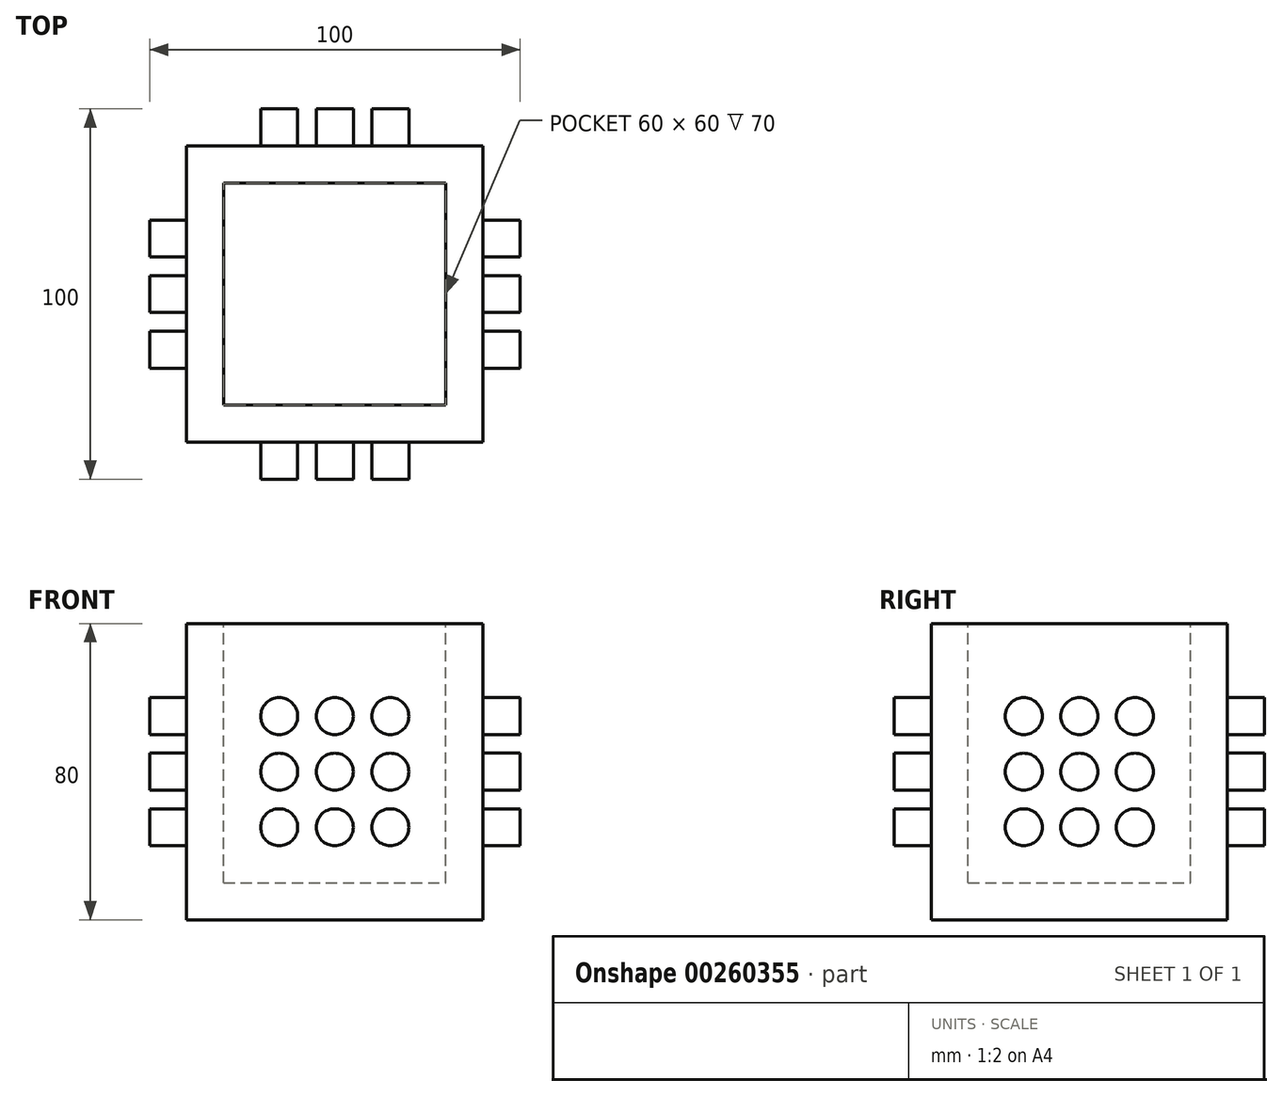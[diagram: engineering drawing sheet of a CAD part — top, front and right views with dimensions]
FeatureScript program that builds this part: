
annotation { "Feature Type Name" : "Feature", "Feature Type Description" : "" }
export const myFeature = defineFeature(function(context is Context, id is Id, definition is map)
    precondition{}
    {
        {
            var Q0;
            Q0=qCreatedBy(makeId("Front.planeOp"),FACE);
            var sketch = newSketch(context, id + "F0", { "sketchPlane" : qUnion([Q0])});
            skLineSegment(sketch, "E0.bottom", {"start": v(0, 0) * mm, "end": v(80, 0) * mm});
            skLineSegment(sketch, "E0.top", {"start": v(0, 80) * mm, "end": v(80, 80) * mm});
            skLineSegment(sketch, "E0.left", {"start": v(0, 0) * mm, "end": v(0, 80) * mm});
            skLineSegment(sketch, "E0.right", {"start": v(80, 0) * mm, "end": v(80, 80) * mm});
            skSolve(sketch);
        }
        {
            var Q0;
            Q0=makeQuery(id+"F0.imprint","IMPRINT",FACE,{"disambiguationData":[TD([[makeQuery(id+"F0.imprint","IMPRINT",EDGE,{"derivedFrom":sQuery(id+"F0.wireOp",EDGE,"E0.bottom")}),1.0]])]});
            extrude(context, id + "F1", {"entities" : qUnion([Q0]), "depth" : 80 * mm});
        }
        {
            var Q0;
            Q0=makeQuery(id+"F1.opExtrude","SWEPT_FACE",FACE,{"disambiguationData":[OSD([sQuery(id+"F0.wireOp",EDGE,"E0.top")])]});
            var sketch = newSketch(context, id + "F2", { "sketchPlane" : qUnion([Q0])});
            skLineSegment(sketch, "E1.bottom", {"start": v(10, -70) * mm, "end": v(70, -70) * mm});
            skLineSegment(sketch, "E1.top", {"start": v(10, -10) * mm, "end": v(70, -10) * mm});
            skLineSegment(sketch, "E1.left", {"start": v(10, -70) * mm, "end": v(10, -10) * mm});
            skLineSegment(sketch, "E1.right", {"start": v(70, -70) * mm, "end": v(70, -10) * mm});
            skSolve(sketch);
        }
        {
            var Q0;
            Q0=makeQuery(id+"F2.imprint","IMPRINT",FACE,{"disambiguationData":[TD([[makeQuery(id+"F2.imprint","IMPRINT",EDGE,{"derivedFrom":sQuery(id+"F2.wireOp",EDGE,"E1.bottom")}),1.0]])]});
            extrude(context, id + "F3", {"entities" : qUnion([Q0]), "operationType" : NewBodyOperationType.REMOVE, "oppositeDirection" : true, "depth" : 70 * mm});
        }
        {
            var Q0;
            Q0=makeQuery(id+"F1.opExtrude","CAP_FACE",FACE,{"disambiguationData":[OSD([sQuery(id+"F0.wireOp",EDGE,"E0.bottom"),sQuery(id+"F0.wireOp",EDGE,"E0.top"),sQuery(id+"F0.wireOp",EDGE,"E0.left"),sQuery(id+"F0.wireOp",EDGE,"E0.right")])],"isStart":false});
            var sketch = newSketch(context, id + "F4", { "sketchPlane" : qUnion([Q0])});
            skLineSegment(sketch, "E2.bottom", {"start": v(10, 10) * mm, "end": v(70, 10) * mm});
            skLineSegment(sketch, "E2.top", {"start": v(10, 70) * mm, "end": v(70, 70) * mm});
            skLineSegment(sketch, "E2.left", {"start": v(10, 10) * mm, "end": v(10, 70) * mm});
            skLineSegment(sketch, "E2.right", {"start": v(70, 10) * mm, "end": v(70, 70) * mm});
            skLineSegment(sketch, "E3", {"start": v(25, 10) * mm, "end": v(25, 20) * mm});
            skLineSegment(sketch, "E4", {"start": v(40, 10) * mm, "end": v(40, 20) * mm});
            skLineSegment(sketch, "E5", {"start": v(55, 10) * mm, "end": v(55, 20) * mm});
            skLineSegment(sketch, "E6", {"start": v(10, 55) * mm, "end": v(20, 55) * mm});
            skLineSegment(sketch, "E7", {"start": v(10, 40) * mm, "end": v(20, 40) * mm});
            skLineSegment(sketch, "E8", {"start": v(10, 25) * mm, "end": v(20, 25) * mm});
            skCircle(sketch, "E9", {"center": v(25, 55) * mm, "radius": 5 * mm});
            skCircle(sketch, "E10", {"center": v(40, 55) * mm, "radius": 5 * mm});
            skCircle(sketch, "E11", {"center": v(55, 55) * mm, "radius": 5 * mm});
            skCircle(sketch, "E12", {"center": v(55, 40) * mm, "radius": 5 * mm});
            skCircle(sketch, "E13", {"center": v(40, 40) * mm, "radius": 5 * mm});
            skCircle(sketch, "E14", {"center": v(25, 40) * mm, "radius": 5 * mm});
            skCircle(sketch, "E15", {"center": v(25, 25) * mm, "radius": 5 * mm});
            skCircle(sketch, "E16", {"center": v(40, 25) * mm, "radius": 5 * mm});
            skCircle(sketch, "E17", {"center": v(55, 25) * mm, "radius": 5 * mm});
            skLineSegment(sketch, "E18.trimOffspring", {"start": v(25, 60) * mm, "end": v(25, 70) * mm});
            skLineSegment(sketch, "E19.trimOffspring", {"start": v(30, 55) * mm, "end": v(35, 55) * mm});
            skLineSegment(sketch, "E20.trimOffspring", {"start": v(45, 55) * mm, "end": v(50, 55) * mm});
            skLineSegment(sketch, "E21.trimOffspring", {"start": v(40, 60) * mm, "end": v(40, 70) * mm});
            skLineSegment(sketch, "E22.trimOffspring", {"start": v(60, 55) * mm, "end": v(70, 55) * mm});
            skLineSegment(sketch, "E23.trimOffspring", {"start": v(55, 60) * mm, "end": v(55, 70) * mm});
            skLineSegment(sketch, "E24.trimOffspring", {"start": v(25, 45) * mm, "end": v(25, 50) * mm});
            skLineSegment(sketch, "E25.trimOffspring", {"start": v(30, 40) * mm, "end": v(35, 40) * mm});
            skLineSegment(sketch, "E26.trimOffspring", {"start": v(45, 40) * mm, "end": v(50, 40) * mm});
            skLineSegment(sketch, "E27.trimOffspring", {"start": v(40, 45) * mm, "end": v(40, 50) * mm});
            skLineSegment(sketch, "E28.trimOffspring", {"start": v(60, 40) * mm, "end": v(70, 40) * mm});
            skLineSegment(sketch, "E29.trimOffspring", {"start": v(55, 45) * mm, "end": v(55, 50) * mm});
            skLineSegment(sketch, "E30.trimOffspring", {"start": v(25, 30) * mm, "end": v(25, 35) * mm});
            skLineSegment(sketch, "E31.trimOffspring", {"start": v(30, 25) * mm, "end": v(35, 25) * mm});
            skLineSegment(sketch, "E32.trimOffspring", {"start": v(45, 25) * mm, "end": v(50, 25) * mm});
            skLineSegment(sketch, "E33.trimOffspring", {"start": v(40, 30) * mm, "end": v(40, 35) * mm});
            skLineSegment(sketch, "E34.trimOffspring", {"start": v(60, 25) * mm, "end": v(70, 25) * mm});
            skLineSegment(sketch, "E35.trimOffspring", {"start": v(55, 30) * mm, "end": v(55, 35) * mm});
            skSolve(sketch);
        }
        {
            var Q0;
            Q0=makeQuery(id+"F1.opExtrude","SWEPT_FACE",FACE,{"disambiguationData":[OSD([sQuery(id+"F0.wireOp",EDGE,"E0.right")])]});
            var sketch = newSketch(context, id + "F5", { "sketchPlane" : qUnion([Q0])});
            skLineSegment(sketch, "E36.bottom", {"start": v(-70, 10) * mm, "end": v(-10, 10) * mm});
            skLineSegment(sketch, "E36.top", {"start": v(-70, 70) * mm, "end": v(-10, 70) * mm});
            skLineSegment(sketch, "E36.left", {"start": v(-70, 10) * mm, "end": v(-70, 70) * mm});
            skLineSegment(sketch, "E36.right", {"start": v(-10, 10) * mm, "end": v(-10, 70) * mm});
            skLineSegment(sketch, "E37", {"start": v(-55, 10) * mm, "end": v(-55, 20) * mm});
            skLineSegment(sketch, "E38", {"start": v(-40, 10) * mm, "end": v(-40, 20) * mm});
            skLineSegment(sketch, "E39", {"start": v(-25, 10) * mm, "end": v(-25, 20) * mm});
            skLineSegment(sketch, "E40", {"start": v(-70, 55) * mm, "end": v(-60, 55) * mm});
            skLineSegment(sketch, "E41", {"start": v(-70, 40) * mm, "end": v(-60, 40) * mm});
            skLineSegment(sketch, "E42", {"start": v(-70, 25) * mm, "end": v(-60, 25) * mm});
            skCircle(sketch, "E43", {"center": v(-55, 55) * mm, "radius": 5 * mm});
            skCircle(sketch, "E44", {"center": v(-40, 55) * mm, "radius": 5 * mm});
            skCircle(sketch, "E45", {"center": v(-25, 55) * mm, "radius": 5 * mm});
            skCircle(sketch, "E46", {"center": v(-25, 40) * mm, "radius": 5 * mm});
            skCircle(sketch, "E47", {"center": v(-40, 40) * mm, "radius": 5 * mm});
            skCircle(sketch, "E48", {"center": v(-55, 40) * mm, "radius": 5 * mm});
            skCircle(sketch, "E49", {"center": v(-55, 25) * mm, "radius": 5 * mm});
            skCircle(sketch, "E50", {"center": v(-40, 25) * mm, "radius": 5 * mm});
            skCircle(sketch, "E51", {"center": v(-25, 25) * mm, "radius": 5 * mm});
            skLineSegment(sketch, "E52.trimOffspring", {"start": v(-55, 60) * mm, "end": v(-55, 70) * mm});
            skLineSegment(sketch, "E53.trimOffspring", {"start": v(-50, 55) * mm, "end": v(-45, 55) * mm});
            skLineSegment(sketch, "E54.trimOffspring", {"start": v(-35, 55) * mm, "end": v(-30, 55) * mm});
            skLineSegment(sketch, "E55.trimOffspring", {"start": v(-40, 60) * mm, "end": v(-40, 70) * mm});
            skLineSegment(sketch, "E56.trimOffspring", {"start": v(-20, 55) * mm, "end": v(-10, 55) * mm});
            skLineSegment(sketch, "E57.trimOffspring", {"start": v(-25, 60) * mm, "end": v(-25, 70) * mm});
            skLineSegment(sketch, "E58.trimOffspring", {"start": v(-55, 45) * mm, "end": v(-55, 50) * mm});
            skLineSegment(sketch, "E59.trimOffspring", {"start": v(-50, 40) * mm, "end": v(-45, 40) * mm});
            skLineSegment(sketch, "E60.trimOffspring", {"start": v(-35, 40) * mm, "end": v(-30, 40) * mm});
            skLineSegment(sketch, "E61.trimOffspring", {"start": v(-40, 45) * mm, "end": v(-40, 50) * mm});
            skLineSegment(sketch, "E62.trimOffspring", {"start": v(-20, 40) * mm, "end": v(-10, 40) * mm});
            skLineSegment(sketch, "E63.trimOffspring", {"start": v(-25, 45) * mm, "end": v(-25, 50) * mm});
            skLineSegment(sketch, "E64.trimOffspring", {"start": v(-55, 30) * mm, "end": v(-55, 35) * mm});
            skLineSegment(sketch, "E65.trimOffspring", {"start": v(-50, 25) * mm, "end": v(-45, 25) * mm});
            skLineSegment(sketch, "E66.trimOffspring", {"start": v(-35, 25) * mm, "end": v(-30, 25) * mm});
            skLineSegment(sketch, "E67.trimOffspring", {"start": v(-40, 30) * mm, "end": v(-40, 35) * mm});
            skLineSegment(sketch, "E68.trimOffspring", {"start": v(-20, 25) * mm, "end": v(-10, 25) * mm});
            skLineSegment(sketch, "E69.trimOffspring", {"start": v(-25, 30) * mm, "end": v(-25, 35) * mm});
            skSolve(sketch);
        }
        {
            var Q0;
            {var subQ0=sQuery(id+"F4.wireOp",EDGE,"E15");var subQ1=makeQuery(id+"F4.imprint","INTERSECT",VERTEX,{"derivedFrom":[subQ0,sQuery(id+"F4.wireOp",EDGE,"E30.trimOffspring")]});Q0=makeQuery(id+"F4.imprint","IMPRINT",FACE,{"disambiguationData":[TD([[makeQuery(id+"F4.imprint","IMPRINT",EDGE,{"disambiguationData":[TD([[subQ1,1.0]])],"derivedFrom":subQ0}),1.0]])]});}
            var Q1;
            {var subQ0=sQuery(id+"F4.wireOp",EDGE,"E16");var subQ1=makeQuery(id+"F4.imprint","INTERSECT",VERTEX,{"derivedFrom":[subQ0,sQuery(id+"F4.wireOp",EDGE,"E32.trimOffspring")]});Q1=makeQuery(id+"F4.imprint","IMPRINT",FACE,{"disambiguationData":[TD([[makeQuery(id+"F4.imprint","IMPRINT",EDGE,{"disambiguationData":[TD([[subQ1,-1.0]])],"derivedFrom":subQ0}),1.0]])]});}
            var Q2;
            {var subQ0=sQuery(id+"F4.wireOp",EDGE,"E17");var subQ1=makeQuery(id+"F4.imprint","INTERSECT",VERTEX,{"derivedFrom":[subQ0,sQuery(id+"F4.wireOp",EDGE,"E34.trimOffspring")]});Q2=makeQuery(id+"F4.imprint","IMPRINT",FACE,{"disambiguationData":[TD([[makeQuery(id+"F4.imprint","IMPRINT",EDGE,{"disambiguationData":[TD([[subQ1,-1.0]])],"derivedFrom":subQ0}),1.0]])]});}
            var Q3;
            {var subQ0=sQuery(id+"F4.wireOp",EDGE,"E12");var subQ1=makeQuery(id+"F4.imprint","INTERSECT",VERTEX,{"derivedFrom":[subQ0,sQuery(id+"F4.wireOp",EDGE,"E28.trimOffspring")]});Q3=makeQuery(id+"F4.imprint","IMPRINT",FACE,{"disambiguationData":[TD([[makeQuery(id+"F4.imprint","IMPRINT",EDGE,{"disambiguationData":[TD([[subQ1,-1.0]])],"derivedFrom":subQ0}),1.0]])]});}
            var Q4;
            {var subQ0=sQuery(id+"F4.wireOp",EDGE,"E13");var subQ1=makeQuery(id+"F4.imprint","INTERSECT",VERTEX,{"derivedFrom":[subQ0,sQuery(id+"F4.wireOp",EDGE,"E26.trimOffspring")]});Q4=makeQuery(id+"F4.imprint","IMPRINT",FACE,{"disambiguationData":[TD([[makeQuery(id+"F4.imprint","IMPRINT",EDGE,{"disambiguationData":[TD([[subQ1,-1.0]])],"derivedFrom":subQ0}),1.0]])]});}
            var Q5;
            {var subQ0=sQuery(id+"F4.wireOp",EDGE,"E14");var subQ1=makeQuery(id+"F4.imprint","INTERSECT",VERTEX,{"derivedFrom":[subQ0,sQuery(id+"F4.wireOp",EDGE,"E24.trimOffspring")]});Q5=makeQuery(id+"F4.imprint","IMPRINT",FACE,{"disambiguationData":[TD([[makeQuery(id+"F4.imprint","IMPRINT",EDGE,{"disambiguationData":[TD([[subQ1,1.0]])],"derivedFrom":subQ0}),1.0]])]});}
            var Q6;
            {var subQ0=sQuery(id+"F4.wireOp",EDGE,"E9");var subQ1=makeQuery(id+"F4.imprint","INTERSECT",VERTEX,{"derivedFrom":[subQ0,sQuery(id+"F4.wireOp",EDGE,"E18.trimOffspring")]});Q6=makeQuery(id+"F4.imprint","IMPRINT",FACE,{"disambiguationData":[TD([[makeQuery(id+"F4.imprint","IMPRINT",EDGE,{"disambiguationData":[TD([[subQ1,1.0]])],"derivedFrom":subQ0}),1.0]])]});}
            var Q7;
            {var subQ0=sQuery(id+"F4.wireOp",EDGE,"E10");var subQ1=makeQuery(id+"F4.imprint","INTERSECT",VERTEX,{"derivedFrom":[subQ0,sQuery(id+"F4.wireOp",EDGE,"E20.trimOffspring")]});Q7=makeQuery(id+"F4.imprint","IMPRINT",FACE,{"disambiguationData":[TD([[makeQuery(id+"F4.imprint","IMPRINT",EDGE,{"disambiguationData":[TD([[subQ1,-1.0]])],"derivedFrom":subQ0}),1.0]])]});}
            var Q8;
            {var subQ0=sQuery(id+"F4.wireOp",EDGE,"E11");var subQ1=makeQuery(id+"F4.imprint","INTERSECT",VERTEX,{"derivedFrom":[subQ0,sQuery(id+"F4.wireOp",EDGE,"E22.trimOffspring")]});Q8=makeQuery(id+"F4.imprint","IMPRINT",FACE,{"disambiguationData":[TD([[makeQuery(id+"F4.imprint","IMPRINT",EDGE,{"disambiguationData":[TD([[subQ1,-1.0]])],"derivedFrom":subQ0}),1.0]])]});}
            extrude(context, id + "F6", {"entities" : qUnion([Q0, Q1, Q2, Q3, Q4, Q5, Q6, Q7, Q8]), "operationType" : NewBodyOperationType.ADD, "depth" : 10 * mm});
        }
        {
            var Q0;
            Q0=makeQuery(id+"F1.opExtrude","CAP_FACE",FACE,{"disambiguationData":[OSD([sQuery(id+"F0.wireOp",EDGE,"E0.bottom"),sQuery(id+"F0.wireOp",EDGE,"E0.top"),sQuery(id+"F0.wireOp",EDGE,"E0.left"),sQuery(id+"F0.wireOp",EDGE,"E0.right")])],"isStart":true});
            var sketch = newSketch(context, id + "F7", { "sketchPlane" : qUnion([Q0])});
            skLineSegment(sketch, "E70.bottom", {"start": v(-70, 10) * mm, "end": v(-10, 10) * mm});
            skLineSegment(sketch, "E70.top", {"start": v(-70, 70) * mm, "end": v(-10, 70) * mm});
            skLineSegment(sketch, "E70.left", {"start": v(-70, 10) * mm, "end": v(-70, 70) * mm});
            skLineSegment(sketch, "E70.right", {"start": v(-10, 10) * mm, "end": v(-10, 70) * mm});
            skLineSegment(sketch, "E71", {"start": v(-55, 10) * mm, "end": v(-55, 20) * mm});
            skLineSegment(sketch, "E72", {"start": v(-40, 10) * mm, "end": v(-40, 20) * mm});
            skLineSegment(sketch, "E73", {"start": v(-25, 10) * mm, "end": v(-25, 20) * mm});
            skLineSegment(sketch, "E74", {"start": v(-70, 55) * mm, "end": v(-60, 55) * mm});
            skLineSegment(sketch, "E75", {"start": v(-70, 40) * mm, "end": v(-60, 40) * mm});
            skLineSegment(sketch, "E76", {"start": v(-70, 25) * mm, "end": v(-60, 25) * mm});
            skCircle(sketch, "E77", {"center": v(-55, 55) * mm, "radius": 5 * mm});
            skCircle(sketch, "E78", {"center": v(-40, 55) * mm, "radius": 5 * mm});
            skCircle(sketch, "E79", {"center": v(-25, 55) * mm, "radius": 5 * mm});
            skCircle(sketch, "E80", {"center": v(-25, 40) * mm, "radius": 5 * mm});
            skCircle(sketch, "E81", {"center": v(-40, 40) * mm, "radius": 5 * mm});
            skCircle(sketch, "E82", {"center": v(-55, 40) * mm, "radius": 5 * mm});
            skCircle(sketch, "E83", {"center": v(-55, 25) * mm, "radius": 5 * mm});
            skCircle(sketch, "E84", {"center": v(-40, 25) * mm, "radius": 5 * mm});
            skCircle(sketch, "E85", {"center": v(-25, 25) * mm, "radius": 5 * mm});
            skLineSegment(sketch, "E86.trimOffspring", {"start": v(-55, 60) * mm, "end": v(-55, 70) * mm});
            skLineSegment(sketch, "E87.trimOffspring", {"start": v(-50, 55) * mm, "end": v(-45, 55) * mm});
            skLineSegment(sketch, "E88.trimOffspring", {"start": v(-35, 55) * mm, "end": v(-30, 55) * mm});
            skLineSegment(sketch, "E89.trimOffspring", {"start": v(-40, 60) * mm, "end": v(-40, 70) * mm});
            skLineSegment(sketch, "E90.trimOffspring", {"start": v(-20, 55) * mm, "end": v(-10, 55) * mm});
            skLineSegment(sketch, "E91.trimOffspring", {"start": v(-25, 60) * mm, "end": v(-25, 70) * mm});
            skLineSegment(sketch, "E92.trimOffspring", {"start": v(-55, 45) * mm, "end": v(-55, 50) * mm});
            skLineSegment(sketch, "E93.trimOffspring", {"start": v(-50, 40) * mm, "end": v(-45, 40) * mm});
            skLineSegment(sketch, "E94.trimOffspring", {"start": v(-35, 40) * mm, "end": v(-30, 40) * mm});
            skLineSegment(sketch, "E95.trimOffspring", {"start": v(-40, 45) * mm, "end": v(-40, 50) * mm});
            skLineSegment(sketch, "E96.trimOffspring", {"start": v(-20, 40) * mm, "end": v(-10, 40) * mm});
            skLineSegment(sketch, "E97.trimOffspring", {"start": v(-25, 45) * mm, "end": v(-25, 50) * mm});
            skLineSegment(sketch, "E98.trimOffspring", {"start": v(-55, 30) * mm, "end": v(-55, 35) * mm});
            skLineSegment(sketch, "E99.trimOffspring", {"start": v(-50, 25) * mm, "end": v(-45, 25) * mm});
            skLineSegment(sketch, "E100.trimOffspring", {"start": v(-35, 25) * mm, "end": v(-30, 25) * mm});
            skLineSegment(sketch, "E101.trimOffspring", {"start": v(-40, 30) * mm, "end": v(-40, 35) * mm});
            skLineSegment(sketch, "E102.trimOffspring", {"start": v(-20, 25) * mm, "end": v(-10, 25) * mm});
            skLineSegment(sketch, "E103.trimOffspring", {"start": v(-25, 30) * mm, "end": v(-25, 35) * mm});
            skSolve(sketch);
        }
        {
            var Q0;
            {var subQ0=sQuery(id+"F7.wireOp",EDGE,"E77");var subQ1=makeQuery(id+"F7.imprint","INTERSECT",VERTEX,{"derivedFrom":[subQ0,sQuery(id+"F7.wireOp",EDGE,"E86.trimOffspring")]});Q0=makeQuery(id+"F7.imprint","IMPRINT",FACE,{"disambiguationData":[TD([[makeQuery(id+"F7.imprint","IMPRINT",EDGE,{"disambiguationData":[TD([[subQ1,1.0]])],"derivedFrom":subQ0}),1.0]])]});}
            var Q1;
            {var subQ0=sQuery(id+"F7.wireOp",EDGE,"E78");var subQ1=makeQuery(id+"F7.imprint","INTERSECT",VERTEX,{"derivedFrom":[subQ0,sQuery(id+"F7.wireOp",EDGE,"E88.trimOffspring")]});Q1=makeQuery(id+"F7.imprint","IMPRINT",FACE,{"disambiguationData":[TD([[makeQuery(id+"F7.imprint","IMPRINT",EDGE,{"disambiguationData":[TD([[subQ1,-1.0]])],"derivedFrom":subQ0}),1.0]])]});}
            var Q2;
            {var subQ0=sQuery(id+"F7.wireOp",EDGE,"E79");var subQ1=makeQuery(id+"F7.imprint","INTERSECT",VERTEX,{"derivedFrom":[subQ0,sQuery(id+"F7.wireOp",EDGE,"E90.trimOffspring")]});Q2=makeQuery(id+"F7.imprint","IMPRINT",FACE,{"disambiguationData":[TD([[makeQuery(id+"F7.imprint","IMPRINT",EDGE,{"disambiguationData":[TD([[subQ1,-1.0]])],"derivedFrom":subQ0}),1.0]])]});}
            var Q3;
            {var subQ0=sQuery(id+"F7.wireOp",EDGE,"E80");var subQ1=makeQuery(id+"F7.imprint","INTERSECT",VERTEX,{"derivedFrom":[subQ0,sQuery(id+"F7.wireOp",EDGE,"E96.trimOffspring")]});Q3=makeQuery(id+"F7.imprint","IMPRINT",FACE,{"disambiguationData":[TD([[makeQuery(id+"F7.imprint","IMPRINT",EDGE,{"disambiguationData":[TD([[subQ1,-1.0]])],"derivedFrom":subQ0}),1.0]])]});}
            var Q4;
            {var subQ0=sQuery(id+"F7.wireOp",EDGE,"E85");var subQ1=makeQuery(id+"F7.imprint","INTERSECT",VERTEX,{"derivedFrom":[subQ0,sQuery(id+"F7.wireOp",EDGE,"E102.trimOffspring")]});Q4=makeQuery(id+"F7.imprint","IMPRINT",FACE,{"disambiguationData":[TD([[makeQuery(id+"F7.imprint","IMPRINT",EDGE,{"disambiguationData":[TD([[subQ1,-1.0]])],"derivedFrom":subQ0}),1.0]])]});}
            var Q5;
            {var subQ0=sQuery(id+"F7.wireOp",EDGE,"E84");var subQ1=makeQuery(id+"F7.imprint","INTERSECT",VERTEX,{"derivedFrom":[subQ0,sQuery(id+"F7.wireOp",EDGE,"E100.trimOffspring")]});Q5=makeQuery(id+"F7.imprint","IMPRINT",FACE,{"disambiguationData":[TD([[makeQuery(id+"F7.imprint","IMPRINT",EDGE,{"disambiguationData":[TD([[subQ1,-1.0]])],"derivedFrom":subQ0}),1.0]])]});}
            var Q6;
            {var subQ0=sQuery(id+"F7.wireOp",EDGE,"E83");var subQ1=makeQuery(id+"F7.imprint","INTERSECT",VERTEX,{"derivedFrom":[subQ0,sQuery(id+"F7.wireOp",EDGE,"E98.trimOffspring")]});Q6=makeQuery(id+"F7.imprint","IMPRINT",FACE,{"disambiguationData":[TD([[makeQuery(id+"F7.imprint","IMPRINT",EDGE,{"disambiguationData":[TD([[subQ1,1.0]])],"derivedFrom":subQ0}),1.0]])]});}
            var Q7;
            {var subQ0=sQuery(id+"F7.wireOp",EDGE,"E82");var subQ1=makeQuery(id+"F7.imprint","INTERSECT",VERTEX,{"derivedFrom":[subQ0,sQuery(id+"F7.wireOp",EDGE,"E92.trimOffspring")]});Q7=makeQuery(id+"F7.imprint","IMPRINT",FACE,{"disambiguationData":[TD([[makeQuery(id+"F7.imprint","IMPRINT",EDGE,{"disambiguationData":[TD([[subQ1,1.0]])],"derivedFrom":subQ0}),1.0]])]});}
            var Q8;
            {var subQ0=sQuery(id+"F7.wireOp",EDGE,"E81");var subQ1=makeQuery(id+"F7.imprint","INTERSECT",VERTEX,{"derivedFrom":[subQ0,sQuery(id+"F7.wireOp",EDGE,"E94.trimOffspring")]});Q8=makeQuery(id+"F7.imprint","IMPRINT",FACE,{"disambiguationData":[TD([[makeQuery(id+"F7.imprint","IMPRINT",EDGE,{"disambiguationData":[TD([[subQ1,-1.0]])],"derivedFrom":subQ0}),1.0]])]});}
            extrude(context, id + "F8", {"entities" : qUnion([Q0, Q1, Q2, Q3, Q4, Q5, Q6, Q7, Q8]), "operationType" : NewBodyOperationType.ADD, "depth" : 10 * mm});
        }
        {
            var Q0;
            {var subQ0=sQuery(id+"F5.wireOp",EDGE,"E43");var subQ1=makeQuery(id+"F5.imprint","INTERSECT",VERTEX,{"derivedFrom":[subQ0,sQuery(id+"F5.wireOp",EDGE,"E52.trimOffspring")]});Q0=makeQuery(id+"F5.imprint","IMPRINT",FACE,{"disambiguationData":[TD([[makeQuery(id+"F5.imprint","IMPRINT",EDGE,{"disambiguationData":[TD([[subQ1,1.0]])],"derivedFrom":subQ0}),1.0]])]});}
            var Q1;
            {var subQ0=sQuery(id+"F5.wireOp",EDGE,"E44");var subQ1=makeQuery(id+"F5.imprint","INTERSECT",VERTEX,{"derivedFrom":[subQ0,sQuery(id+"F5.wireOp",EDGE,"E54.trimOffspring")]});Q1=makeQuery(id+"F5.imprint","IMPRINT",FACE,{"disambiguationData":[TD([[makeQuery(id+"F5.imprint","IMPRINT",EDGE,{"disambiguationData":[TD([[subQ1,-1.0]])],"derivedFrom":subQ0}),1.0]])]});}
            var Q2;
            {var subQ0=sQuery(id+"F5.wireOp",EDGE,"E45");var subQ1=makeQuery(id+"F5.imprint","INTERSECT",VERTEX,{"derivedFrom":[subQ0,sQuery(id+"F5.wireOp",EDGE,"E56.trimOffspring")]});Q2=makeQuery(id+"F5.imprint","IMPRINT",FACE,{"disambiguationData":[TD([[makeQuery(id+"F5.imprint","IMPRINT",EDGE,{"disambiguationData":[TD([[subQ1,-1.0]])],"derivedFrom":subQ0}),1.0]])]});}
            var Q3;
            {var subQ0=sQuery(id+"F5.wireOp",EDGE,"E46");var subQ1=makeQuery(id+"F5.imprint","INTERSECT",VERTEX,{"derivedFrom":[subQ0,sQuery(id+"F5.wireOp",EDGE,"E62.trimOffspring")]});Q3=makeQuery(id+"F5.imprint","IMPRINT",FACE,{"disambiguationData":[TD([[makeQuery(id+"F5.imprint","IMPRINT",EDGE,{"disambiguationData":[TD([[subQ1,-1.0]])],"derivedFrom":subQ0}),1.0]])]});}
            var Q4;
            {var subQ0=sQuery(id+"F5.wireOp",EDGE,"E51");var subQ1=makeQuery(id+"F5.imprint","INTERSECT",VERTEX,{"derivedFrom":[subQ0,sQuery(id+"F5.wireOp",EDGE,"E68.trimOffspring")]});Q4=makeQuery(id+"F5.imprint","IMPRINT",FACE,{"disambiguationData":[TD([[makeQuery(id+"F5.imprint","IMPRINT",EDGE,{"disambiguationData":[TD([[subQ1,-1.0]])],"derivedFrom":subQ0}),1.0]])]});}
            var Q5;
            {var subQ0=sQuery(id+"F5.wireOp",EDGE,"E50");var subQ1=makeQuery(id+"F5.imprint","INTERSECT",VERTEX,{"derivedFrom":[subQ0,sQuery(id+"F5.wireOp",EDGE,"E66.trimOffspring")]});Q5=makeQuery(id+"F5.imprint","IMPRINT",FACE,{"disambiguationData":[TD([[makeQuery(id+"F5.imprint","IMPRINT",EDGE,{"disambiguationData":[TD([[subQ1,-1.0]])],"derivedFrom":subQ0}),1.0]])]});}
            var Q6;
            {var subQ0=sQuery(id+"F5.wireOp",EDGE,"E47");var subQ1=makeQuery(id+"F5.imprint","INTERSECT",VERTEX,{"derivedFrom":[subQ0,sQuery(id+"F5.wireOp",EDGE,"E60.trimOffspring")]});Q6=makeQuery(id+"F5.imprint","IMPRINT",FACE,{"disambiguationData":[TD([[makeQuery(id+"F5.imprint","IMPRINT",EDGE,{"disambiguationData":[TD([[subQ1,-1.0]])],"derivedFrom":subQ0}),1.0]])]});}
            var Q7;
            {var subQ0=sQuery(id+"F5.wireOp",EDGE,"E48");var subQ1=makeQuery(id+"F5.imprint","INTERSECT",VERTEX,{"derivedFrom":[subQ0,sQuery(id+"F5.wireOp",EDGE,"E58.trimOffspring")]});Q7=makeQuery(id+"F5.imprint","IMPRINT",FACE,{"disambiguationData":[TD([[makeQuery(id+"F5.imprint","IMPRINT",EDGE,{"disambiguationData":[TD([[subQ1,1.0]])],"derivedFrom":subQ0}),1.0]])]});}
            var Q8;
            {var subQ0=sQuery(id+"F5.wireOp",EDGE,"E49");var subQ1=makeQuery(id+"F5.imprint","INTERSECT",VERTEX,{"derivedFrom":[subQ0,sQuery(id+"F5.wireOp",EDGE,"E64.trimOffspring")]});Q8=makeQuery(id+"F5.imprint","IMPRINT",FACE,{"disambiguationData":[TD([[makeQuery(id+"F5.imprint","IMPRINT",EDGE,{"disambiguationData":[TD([[subQ1,1.0]])],"derivedFrom":subQ0}),1.0]])]});}
            extrude(context, id + "F9", {"entities" : qUnion([Q0, Q1, Q2, Q3, Q4, Q5, Q6, Q7, Q8]), "operationType" : NewBodyOperationType.ADD, "depth" : 10 * mm});
        }
        {
            var Q0;
            Q0=makeQuery(id+"F1.opExtrude","SWEPT_FACE",FACE,{"disambiguationData":[OSD([sQuery(id+"F0.wireOp",EDGE,"E0.left")])]});
            var sketch = newSketch(context, id + "F10", { "sketchPlane" : qUnion([Q0])});
            skLineSegment(sketch, "E104.bottom", {"start": v(10, 10) * mm, "end": v(70, 10) * mm});
            skLineSegment(sketch, "E104.top", {"start": v(10, 70) * mm, "end": v(70, 70) * mm});
            skLineSegment(sketch, "E104.left", {"start": v(10, 10) * mm, "end": v(10, 70) * mm});
            skLineSegment(sketch, "E104.right", {"start": v(70, 10) * mm, "end": v(70, 70) * mm});
            skLineSegment(sketch, "E105", {"start": v(25, 10) * mm, "end": v(25, 20) * mm});
            skLineSegment(sketch, "E106", {"start": v(40, 10) * mm, "end": v(40, 20) * mm});
            skLineSegment(sketch, "E107", {"start": v(55, 10) * mm, "end": v(55, 20) * mm});
            skLineSegment(sketch, "E108", {"start": v(10, 55) * mm, "end": v(20, 55) * mm});
            skLineSegment(sketch, "E109", {"start": v(10, 40) * mm, "end": v(20, 40) * mm});
            skLineSegment(sketch, "E110", {"start": v(10, 25) * mm, "end": v(20, 25) * mm});
            skCircle(sketch, "E111", {"center": v(25, 55) * mm, "radius": 5 * mm});
            skCircle(sketch, "E112", {"center": v(40, 55) * mm, "radius": 5 * mm});
            skCircle(sketch, "E113", {"center": v(55, 55) * mm, "radius": 5 * mm});
            skCircle(sketch, "E114", {"center": v(55, 40) * mm, "radius": 5 * mm});
            skCircle(sketch, "E115", {"center": v(40, 40) * mm, "radius": 5 * mm});
            skCircle(sketch, "E116", {"center": v(25, 40) * mm, "radius": 5 * mm});
            skCircle(sketch, "E117", {"center": v(25, 25) * mm, "radius": 5 * mm});
            skCircle(sketch, "E118", {"center": v(40, 25) * mm, "radius": 5 * mm});
            skCircle(sketch, "E119", {"center": v(55, 25) * mm, "radius": 5 * mm});
            skLineSegment(sketch, "E120.trimOffspring", {"start": v(25, 60) * mm, "end": v(25, 70) * mm});
            skLineSegment(sketch, "E121.trimOffspring", {"start": v(30, 55) * mm, "end": v(35, 55) * mm});
            skLineSegment(sketch, "E122.trimOffspring", {"start": v(45, 55) * mm, "end": v(50, 55) * mm});
            skLineSegment(sketch, "E123.trimOffspring", {"start": v(40, 60) * mm, "end": v(40, 70) * mm});
            skLineSegment(sketch, "E124.trimOffspring", {"start": v(60, 55) * mm, "end": v(70, 55) * mm});
            skLineSegment(sketch, "E125.trimOffspring", {"start": v(55, 60) * mm, "end": v(55, 70) * mm});
            skLineSegment(sketch, "E126.trimOffspring", {"start": v(25, 45) * mm, "end": v(25, 50) * mm});
            skLineSegment(sketch, "E127.trimOffspring", {"start": v(30, 40) * mm, "end": v(35, 40) * mm});
            skLineSegment(sketch, "E128.trimOffspring", {"start": v(45, 40) * mm, "end": v(50, 40) * mm});
            skLineSegment(sketch, "E129.trimOffspring", {"start": v(40, 45) * mm, "end": v(40, 50) * mm});
            skLineSegment(sketch, "E130.trimOffspring", {"start": v(60, 40) * mm, "end": v(70, 40) * mm});
            skLineSegment(sketch, "E131.trimOffspring", {"start": v(55, 45) * mm, "end": v(55, 50) * mm});
            skLineSegment(sketch, "E132.trimOffspring", {"start": v(25, 30) * mm, "end": v(25, 35) * mm});
            skLineSegment(sketch, "E133.trimOffspring", {"start": v(30, 25) * mm, "end": v(35, 25) * mm});
            skLineSegment(sketch, "E134.trimOffspring", {"start": v(45, 25) * mm, "end": v(50, 25) * mm});
            skLineSegment(sketch, "E135.trimOffspring", {"start": v(40, 30) * mm, "end": v(40, 35) * mm});
            skLineSegment(sketch, "E136.trimOffspring", {"start": v(60, 25) * mm, "end": v(70, 25) * mm});
            skLineSegment(sketch, "E137.trimOffspring", {"start": v(55, 30) * mm, "end": v(55, 35) * mm});
            skSolve(sketch);
        }
        {
            var Q0;
            {var subQ0=sQuery(id+"F10.wireOp",EDGE,"E111");var subQ1=makeQuery(id+"F10.imprint","INTERSECT",VERTEX,{"derivedFrom":[subQ0,sQuery(id+"F10.wireOp",EDGE,"E120.trimOffspring")]});Q0=makeQuery(id+"F10.imprint","IMPRINT",FACE,{"disambiguationData":[TD([[makeQuery(id+"F10.imprint","IMPRINT",EDGE,{"disambiguationData":[TD([[subQ1,1.0]])],"derivedFrom":subQ0}),1.0]])]});}
            var Q1;
            {var subQ0=sQuery(id+"F10.wireOp",EDGE,"E112");var subQ1=makeQuery(id+"F10.imprint","INTERSECT",VERTEX,{"derivedFrom":[subQ0,sQuery(id+"F10.wireOp",EDGE,"E122.trimOffspring")]});Q1=makeQuery(id+"F10.imprint","IMPRINT",FACE,{"disambiguationData":[TD([[makeQuery(id+"F10.imprint","IMPRINT",EDGE,{"disambiguationData":[TD([[subQ1,-1.0]])],"derivedFrom":subQ0}),1.0]])]});}
            var Q2;
            {var subQ0=sQuery(id+"F10.wireOp",EDGE,"E113");var subQ1=makeQuery(id+"F10.imprint","INTERSECT",VERTEX,{"derivedFrom":[subQ0,sQuery(id+"F10.wireOp",EDGE,"E124.trimOffspring")]});Q2=makeQuery(id+"F10.imprint","IMPRINT",FACE,{"disambiguationData":[TD([[makeQuery(id+"F10.imprint","IMPRINT",EDGE,{"disambiguationData":[TD([[subQ1,-1.0]])],"derivedFrom":subQ0}),1.0]])]});}
            var Q3;
            {var subQ0=sQuery(id+"F10.wireOp",EDGE,"E116");var subQ1=makeQuery(id+"F10.imprint","INTERSECT",VERTEX,{"derivedFrom":[subQ0,sQuery(id+"F10.wireOp",EDGE,"E126.trimOffspring")]});Q3=makeQuery(id+"F10.imprint","IMPRINT",FACE,{"disambiguationData":[TD([[makeQuery(id+"F10.imprint","IMPRINT",EDGE,{"disambiguationData":[TD([[subQ1,1.0]])],"derivedFrom":subQ0}),1.0]])]});}
            var Q4;
            {var subQ0=sQuery(id+"F10.wireOp",EDGE,"E115");var subQ1=makeQuery(id+"F10.imprint","INTERSECT",VERTEX,{"derivedFrom":[subQ0,sQuery(id+"F10.wireOp",EDGE,"E128.trimOffspring")]});Q4=makeQuery(id+"F10.imprint","IMPRINT",FACE,{"disambiguationData":[TD([[makeQuery(id+"F10.imprint","IMPRINT",EDGE,{"disambiguationData":[TD([[subQ1,-1.0]])],"derivedFrom":subQ0}),1.0]])]});}
            var Q5;
            {var subQ0=sQuery(id+"F10.wireOp",EDGE,"E119");var subQ1=makeQuery(id+"F10.imprint","INTERSECT",VERTEX,{"derivedFrom":[subQ0,sQuery(id+"F10.wireOp",EDGE,"E136.trimOffspring")]});Q5=makeQuery(id+"F10.imprint","IMPRINT",FACE,{"disambiguationData":[TD([[makeQuery(id+"F10.imprint","IMPRINT",EDGE,{"disambiguationData":[TD([[subQ1,-1.0]])],"derivedFrom":subQ0}),1.0]])]});}
            var Q6;
            {var subQ0=sQuery(id+"F10.wireOp",EDGE,"E118");var subQ1=makeQuery(id+"F10.imprint","INTERSECT",VERTEX,{"derivedFrom":[subQ0,sQuery(id+"F10.wireOp",EDGE,"E134.trimOffspring")]});Q6=makeQuery(id+"F10.imprint","IMPRINT",FACE,{"disambiguationData":[TD([[makeQuery(id+"F10.imprint","IMPRINT",EDGE,{"disambiguationData":[TD([[subQ1,-1.0]])],"derivedFrom":subQ0}),1.0]])]});}
            var Q7;
            {var subQ0=sQuery(id+"F10.wireOp",EDGE,"E117");var subQ1=makeQuery(id+"F10.imprint","INTERSECT",VERTEX,{"derivedFrom":[subQ0,sQuery(id+"F10.wireOp",EDGE,"E132.trimOffspring")]});Q7=makeQuery(id+"F10.imprint","IMPRINT",FACE,{"disambiguationData":[TD([[makeQuery(id+"F10.imprint","IMPRINT",EDGE,{"disambiguationData":[TD([[subQ1,1.0]])],"derivedFrom":subQ0}),1.0]])]});}
            var Q8;
            {var subQ0=sQuery(id+"F10.wireOp",EDGE,"E114");var subQ1=makeQuery(id+"F10.imprint","INTERSECT",VERTEX,{"derivedFrom":[subQ0,sQuery(id+"F10.wireOp",EDGE,"E130.trimOffspring")]});Q8=makeQuery(id+"F10.imprint","IMPRINT",FACE,{"disambiguationData":[TD([[makeQuery(id+"F10.imprint","IMPRINT",EDGE,{"disambiguationData":[TD([[subQ1,-1.0]])],"derivedFrom":subQ0}),1.0]])]});}
            extrude(context, id + "F11", {"entities" : qUnion([Q0, Q1, Q2, Q3, Q4, Q5, Q6, Q7, Q8]), "operationType" : NewBodyOperationType.ADD, "depth" : 10 * mm});
        }
    });
